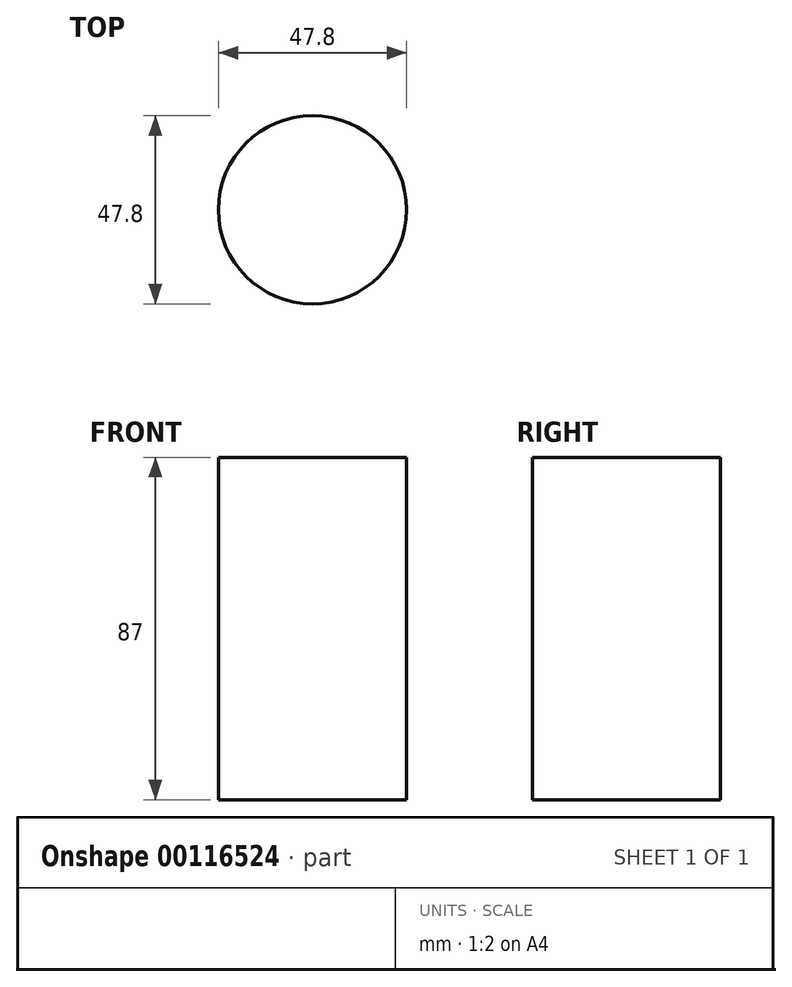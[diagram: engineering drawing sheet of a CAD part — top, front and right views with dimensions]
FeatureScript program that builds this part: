
annotation { "Feature Type Name" : "Feature", "Feature Type Description" : "" }
export const myFeature = defineFeature(function(context is Context, id is Id, definition is map)
    precondition{}
    {
        {
            var Q0;
            Q0=qCreatedBy(makeId("Top.planeOp"),FACE);
            var sketch = newSketch(context, id + "F0", { "sketchPlane" : qUnion([Q0])});
            skCircle(sketch, "E0", {"center": v(0, 0) * mm, "radius": 23.9 * mm});
            skSolve(sketch);
        }
        {
            var Q0;
            Q0=qSketchRegion(id+"F0",true);
            var Q1;
            Q1=makeQuery(id+"F0.imprint","IMPRINT",FACE,{"disambiguationData":[TD([[makeQuery(id+"F0.imprint","IMPRINT",EDGE,{"derivedFrom":sQuery(id+"F0.wireOp",EDGE,"E0")}),1.0]])]});
            extrude(context, id + "F1", {"entities" : qUnion([Q0, Q1]), "depth" : 87 * mm});
        }
    });
